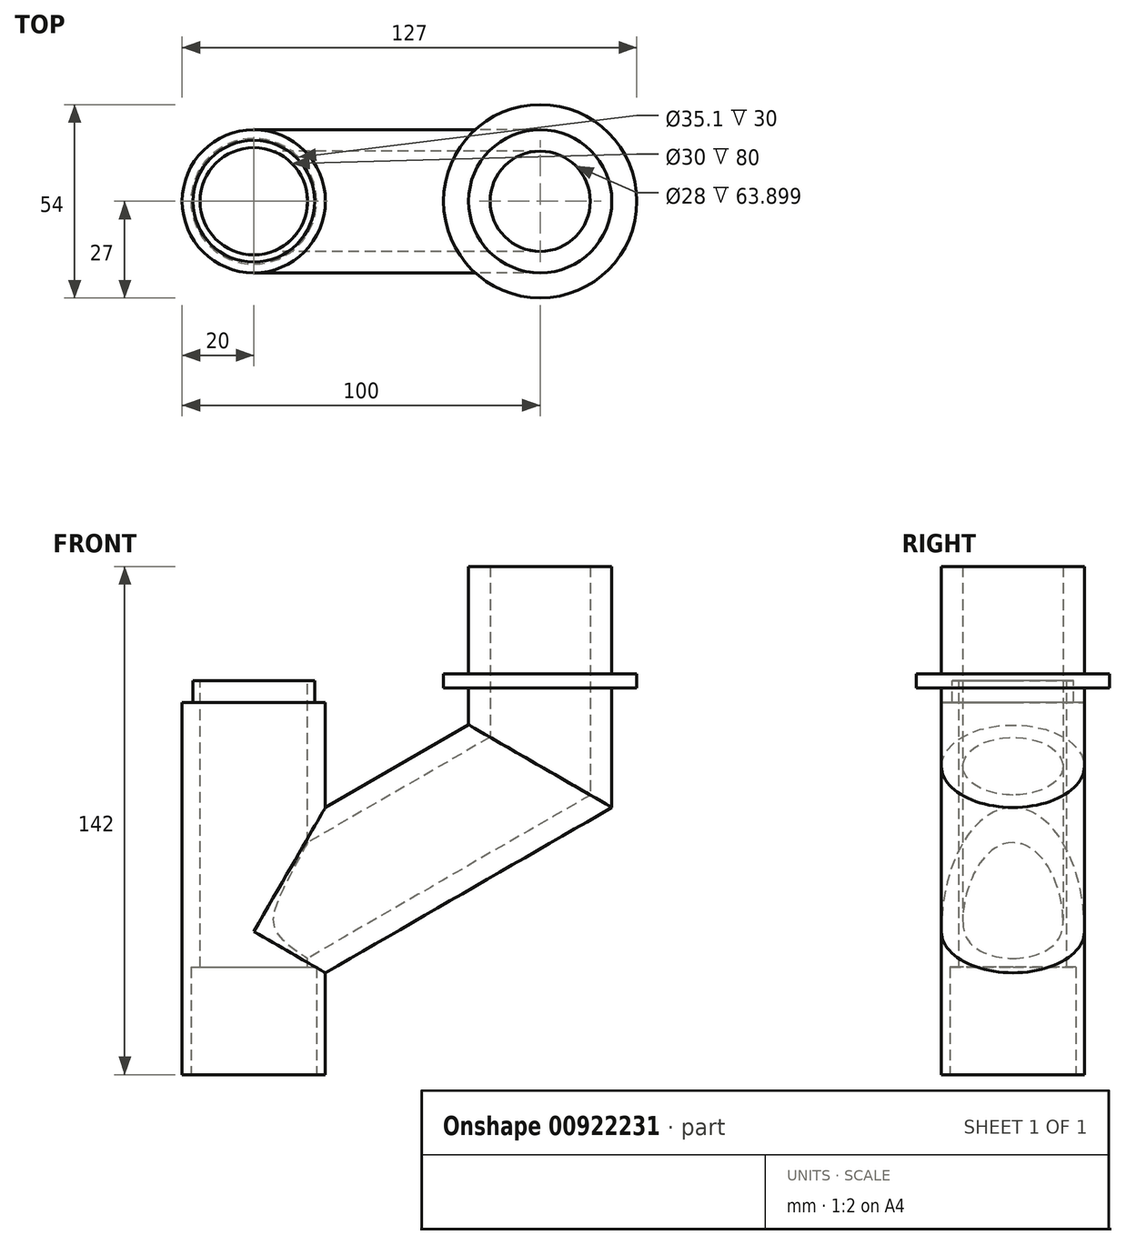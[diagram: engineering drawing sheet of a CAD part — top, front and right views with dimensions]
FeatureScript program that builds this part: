
annotation { "Feature Type Name" : "Feature", "Feature Type Description" : "" }
export const myFeature = defineFeature(function(context is Context, id is Id, definition is map)
    precondition{}
    {
        {
            var Q0;
            Q0=qCreatedBy(makeId("Front.planeOp"),FACE);
            var sketch = newSketch(context, id + "F0", { "sketchPlane" : qUnion([Q0])});
            skLineSegment(sketch, "E0", {"start": v(0, 0) * mm, "end": v(0, -70) * mm});
            skLineSegment(sketch, "E1", {"start": v(0, -70) * mm, "end": v(80, -23.81) * mm});
            skLineSegment(sketch, "E2", {"start": v(80, -23.81) * mm, "end": v(80, 0) * mm});
            skLineSegment(sketch, "E3", {"start": v(0, -70) * mm, "end": v(0, -110) * mm});
            skLineSegment(sketch, "E4", {"start": v(0, 0) * mm, "end": v(0, -23.81) * mm});
            skLineSegment(sketch, "E5", {"start": v(0, -23.81) * mm, "end": v(0, -70) * mm});
            skSolve(sketch);
        }
        {
            var Q0;
            Q0=qCreatedBy(makeId("Top.planeOp"),FACE);
            var sketch = newSketch(context, id + "F1", { "sketchPlane" : qUnion([Q0])});
            skCircle(sketch, "E6", {"center": v(0, 0) * mm, "radius": 20 * mm});
            skCircle(sketch, "E7", {"center": v(80, 0) * mm, "radius": 20 * mm});
            skSolve(sketch);
        }
        {
            var Q0;
            Q0=makeQuery(id+"F1.imprint","IMPRINT",FACE,{"disambiguationData":[TD([[makeQuery(id+"F1.imprint","IMPRINT",EDGE,{"derivedFrom":sQuery(id+"F1.wireOp",EDGE,"E6")}),1.0]])]});
            var Q1;
            Q1=sQuery(id+"F0.wireOp",EDGE,"E0");
            var Q2;
            Q2=sQuery(id+"F0.wireOp",EDGE,"E3");
            sweep(context, id + "F2", {"profiles" : qUnion([Q0]), "path" : qUnion([Q1, Q2])});
        }
        {
            var Q0;
            Q0=makeQuery(id+"F1.imprint","IMPRINT",FACE,{"disambiguationData":[TD([[makeQuery(id+"F1.imprint","IMPRINT",EDGE,{"derivedFrom":sQuery(id+"F1.wireOp",EDGE,"E7")}),1.0]])]});
            var Q1;
            Q1=sQuery(id+"F0.wireOp",EDGE,"E2");
            var Q2;
            Q2=sQuery(id+"F0.wireOp",EDGE,"E1");
            sweep(context, id + "F3", {"operationType" : NewBodyOperationType.ADD, "profiles" : qUnion([Q0]), "path" : qUnion([Q1, Q2])});
        }
        {
            var Q0;
            Q0=makeQuery(id+"F2.opSweep","CAP_FACE",FACE,{"disambiguationData":[OSD([sQuery(id+"F0.wireOp",VERTEX,"E3.end"),sQuery(id+"F1.wireOp",EDGE,"E6")])],"isStart":false});
            var sketch = newSketch(context, id + "F4", { "sketchPlane" : qUnion([Q0])});
            skCircle(sketch, "E8", {"center": v(0, 0) * mm, "radius": 17.55 * mm});
            skSolve(sketch);
        }
        {
            var Q0;
            Q0=qSketchRegion(id+"F4",true);
            extrude(context, id + "F5", {"entities" : qUnion([Q0]), "operationType" : NewBodyOperationType.REMOVE, "oppositeDirection" : true, "depth" : 30 * mm, "offsetDistance" : 25 * mm});
        }
        {
            var Q0;
            Q0=makeQuery(id+"F1.imprint","IMPRINT",FACE,{"disambiguationData":[TD([[makeQuery(id+"F1.imprint","IMPRINT",EDGE,{"derivedFrom":sQuery(id+"F1.wireOp",EDGE,"E6")}),1.0]])]});
            var sketch = newSketch(context, id + "F6", { "sketchPlane" : qUnion([Q0])});
            skCircle(sketch, "E9", {"center": v(0, 0) * mm, "radius": 15 * mm});
            skSolve(sketch);
        }
        {
            var Q0;
            Q0=makeQuery(id+"F6.imprint","IMPRINT",FACE,{"disambiguationData":[TD([[makeQuery(id+"F6.imprint","IMPRINT",EDGE,{"derivedFrom":sQuery(id+"F6.wireOp",EDGE,"E9")}),1.0]])]});
            extrude(context, id + "F7", {"entities" : qUnion([Q0]), "operationType" : NewBodyOperationType.REMOVE, "endBound" : BoundingType.THROUGH_ALL, "oppositeDirection" : true, "depth" : 25 * mm, "offsetDistance" : 25 * mm});
        }
        {
            var Q0;
            Q0=makeQuery(id+"F1.imprint","IMPRINT",FACE,{"disambiguationData":[TD([[makeQuery(id+"F1.imprint","IMPRINT",EDGE,{"derivedFrom":sQuery(id+"F1.wireOp",EDGE,"E6")}),1.0]])]});
            var sketch = newSketch(context, id + "F8", { "sketchPlane" : qUnion([Q0])});
            skCircle(sketch, "E10", {"center": v(0, 0) * mm, "radius": 17 * mm});
            skCircle(sketch, "E11", {"center": v(0, 0) * mm, "radius": 20 * mm});
            skSolve(sketch);
        }
        {
            var Q0;
            Q0=makeQuery(id+"F8.imprint","IMPRINT",FACE,{"disambiguationData":[TD([[makeQuery(id+"F8.imprint","IMPRINT",EDGE,{"derivedFrom":sQuery(id+"F8.wireOp",EDGE,"E10")}),-1.0]])]});
            extrude(context, id + "F9", {"entities" : qUnion([Q0]), "operationType" : NewBodyOperationType.REMOVE, "oppositeDirection" : true, "depth" : 6 * mm, "offsetDistance" : 25 * mm});
        }
        {
            var Q0;
            Q0=makeQuery(id+"F1.imprint","IMPRINT",FACE,{"disambiguationData":[TD([[makeQuery(id+"F1.imprint","IMPRINT",EDGE,{"derivedFrom":sQuery(id+"F1.wireOp",EDGE,"E7")}),1.0]])]});
            var sketch = newSketch(context, id + "F10", { "sketchPlane" : qUnion([Q0])});
            skCircle(sketch, "E12", {"center": v(80, 0) * mm, "radius": 14 * mm});
            skSolve(sketch);
        }
        {
            var Q0;
            Q0=makeQuery(id+"F10.imprint","IMPRINT",FACE,{"disambiguationData":[TD([[makeQuery(id+"F10.imprint","IMPRINT",EDGE,{"derivedFrom":sQuery(id+"F10.wireOp",EDGE,"E12")}),1.0]])]});
            var Q1;
            Q1=sQuery(id+"F0.wireOp",EDGE,"E2");
            var Q2;
            Q2=sQuery(id+"F0.wireOp",EDGE,"E1");
            sweep(context, id + "F11", {"operationType" : NewBodyOperationType.REMOVE, "profiles" : qUnion([Q0]), "path" : qUnion([Q1, Q2])});
        }
        {
            var Q0;
            Q0=makeQuery(id+"F1.imprint","IMPRINT",FACE,{"disambiguationData":[TD([[makeQuery(id+"F1.imprint","IMPRINT",EDGE,{"derivedFrom":sQuery(id+"F1.wireOp",EDGE,"E7")}),1.0]])]});
            var sketch = newSketch(context, id + "F12", { "sketchPlane" : qUnion([Q0])});
            skCircle(sketch, "E13", {"center": v(80, 0) * mm, "radius": 27 * mm});
            skCircle(sketch, "E14", {"center": v(80, 0) * mm, "radius": 20 * mm});
            skCircle(sketch, "E15", {"center": v(80, 0) * mm, "radius": 14 * mm});
            skSolve(sketch);
        }
        {
            var Q0;
            Q0=makeQuery(id+"F12.imprint","IMPRINT",FACE,{"disambiguationData":[TD([[makeQuery(id+"F12.imprint","IMPRINT",EDGE,{"derivedFrom":sQuery(id+"F12.wireOp",EDGE,"E13")}),1.0]])]});
            extrude(context, id + "F13", {"entities" : qUnion([Q0]), "operationType" : NewBodyOperationType.ADD, "endBound" : BoundingType.SYMMETRIC, "depth" : 4 * mm, "offsetDistance" : 25 * mm});
        }
        {
            var Q0;
            Q0=makeQuery(id+"F1.imprint","IMPRINT",FACE,{"disambiguationData":[TD([[makeQuery(id+"F1.imprint","IMPRINT",EDGE,{"derivedFrom":sQuery(id+"F1.wireOp",EDGE,"E7")}),1.0]])]});
            extrude(context, id + "F14", {"entities" : qUnion([Q0]), "operationType" : NewBodyOperationType.ADD, "depth" : 32 * mm, "offsetDistance" : 25 * mm});
        }
        {
            var Q0;
            Q0=makeQuery(id+"F14.opExtrude","CAP_FACE",FACE,{"disambiguationData":[OSD([sQuery(id+"F1.wireOp",EDGE,"E7")])],"isStart":false});
            var sketch = newSketch(context, id + "F15", { "sketchPlane" : qUnion([Q0])});
            skCircle(sketch, "E16", {"center": v(80, 0) * mm, "radius": 14 * mm});
            skSolve(sketch);
        }
        {
            var Q0;
            Q0=makeQuery(id+"F15.imprint","IMPRINT",FACE,{"disambiguationData":[TD([[makeQuery(id+"F15.imprint","IMPRINT",EDGE,{"derivedFrom":sQuery(id+"F15.wireOp",EDGE,"E16")}),1.0]])]});
            extrude(context, id + "F16", {"entities" : qUnion([Q0]), "operationType" : NewBodyOperationType.REMOVE, "oppositeDirection" : true, "depth" : 34 * mm, "offsetDistance" : 25 * mm});
        }
    });
